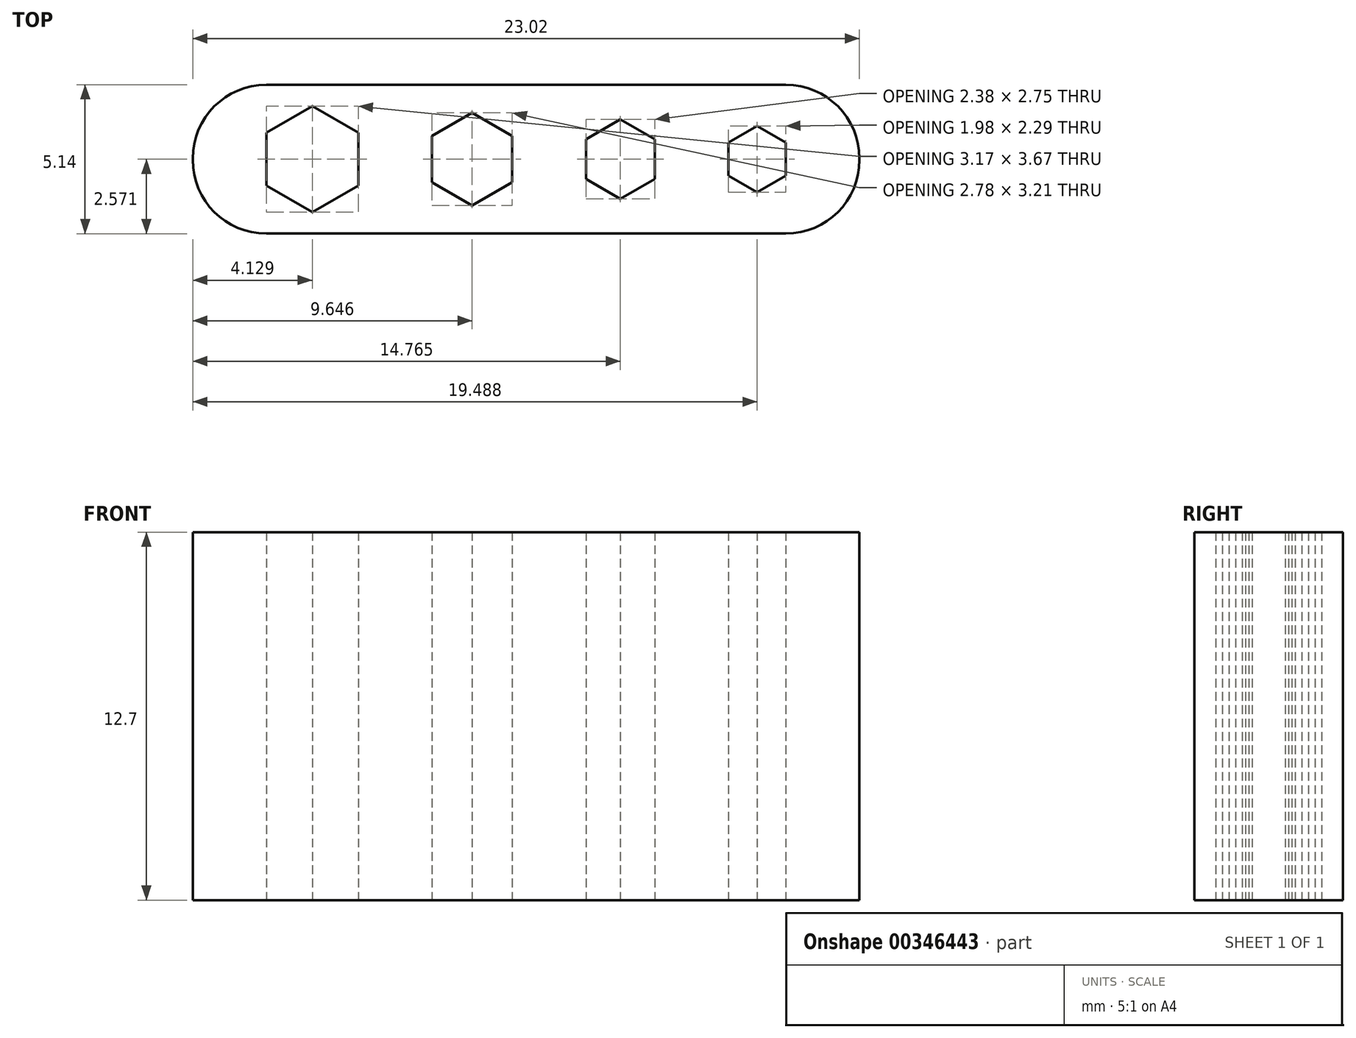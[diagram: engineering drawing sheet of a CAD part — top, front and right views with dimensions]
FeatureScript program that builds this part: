
annotation { "Feature Type Name" : "Feature", "Feature Type Description" : "" }
export const myFeature = defineFeature(function(context is Context, id is Id, definition is map)
    precondition{}
    {
        {
            var Q0;
            Q0=qCreatedBy(makeId("Top.planeOp"),FACE);
            var sketch = newSketch(context, id + "F0", { "sketchPlane" : qUnion([Q0])});
            skLineSegment(sketch, "E0.bottom", {"start": v(7.75, 15.33) * mm, "end": v(30.77, 15.33) * mm});
            skLineSegment(sketch, "E0.top", {"start": v(7.75, 10.2) * mm, "end": v(30.77, 10.2) * mm});
            skLineSegment(sketch, "E0.left", {"start": v(7.75, 15.33) * mm, "end": v(7.75, 10.2) * mm});
            skLineSegment(sketch, "E0.right", {"start": v(30.77, 15.33) * mm, "end": v(30.77, 10.2) * mm});
            skPoint(sketch, "E1.cCircle.centerSnap0", {"position": v(7.75, 12.76) * mm});
            skCircle(sketch, "E2.cCircle", {"center": v(22.52, 12.76) * mm, "radius": 1.2 * mm, "construction": true});
            skLineSegment(sketch, "E2.0", {"start": v(23.7, 13.45) * mm, "end": v(23.7, 12.07) * mm});
            skLineSegment(sketch, "E2.1", {"start": v(23.7, 12.07) * mm, "end": v(22.52, 11.39) * mm});
            skLineSegment(sketch, "E2.2", {"start": v(22.52, 11.39) * mm, "end": v(21.32, 12.07) * mm});
            skLineSegment(sketch, "E2.3", {"start": v(21.32, 12.07) * mm, "end": v(21.32, 13.45) * mm});
            skLineSegment(sketch, "E2.4", {"start": v(21.32, 13.45) * mm, "end": v(22.52, 14.14) * mm});
            skLineSegment(sketch, "E2.5", {"start": v(22.52, 14.14) * mm, "end": v(23.7, 13.45) * mm});
            skPoint(sketch, "E2.0.midPoint", {"position": v(23.7, 12.76) * mm});
            skCircle(sketch, "E3.cCircle", {"center": v(27.24, 12.76) * mm, "radius": 1 * mm, "construction": true});
            skLineSegment(sketch, "E3.0", {"start": v(28.23, 13.33) * mm, "end": v(28.23, 12.19) * mm});
            skLineSegment(sketch, "E3.1", {"start": v(28.23, 12.19) * mm, "end": v(27.24, 11.62) * mm});
            skLineSegment(sketch, "E3.2", {"start": v(27.24, 11.62) * mm, "end": v(26.25, 12.19) * mm});
            skLineSegment(sketch, "E3.3", {"start": v(26.25, 12.19) * mm, "end": v(26.25, 13.33) * mm});
            skLineSegment(sketch, "E3.4", {"start": v(26.25, 13.33) * mm, "end": v(27.24, 13.9) * mm});
            skLineSegment(sketch, "E3.5", {"start": v(27.24, 13.9) * mm, "end": v(28.23, 13.33) * mm});
            skPoint(sketch, "E3.0.midPoint", {"position": v(28.23, 12.76) * mm});
            skCircle(sketch, "E4.cCircle", {"center": v(11.88, 12.76) * mm, "radius": 1.59 * mm, "construction": true});
            skLineSegment(sketch, "E4.0", {"start": v(13.47, 13.68) * mm, "end": v(13.47, 11.84) * mm});
            skLineSegment(sketch, "E4.1", {"start": v(13.47, 11.84) * mm, "end": v(11.88, 10.93) * mm});
            skLineSegment(sketch, "E4.2", {"start": v(11.88, 10.93) * mm, "end": v(10.3, 11.84) * mm});
            skLineSegment(sketch, "E4.3", {"start": v(10.3, 11.84) * mm, "end": v(10.3, 13.68) * mm});
            skLineSegment(sketch, "E4.4", {"start": v(10.3, 13.68) * mm, "end": v(11.88, 14.6) * mm});
            skLineSegment(sketch, "E4.5", {"start": v(11.88, 14.6) * mm, "end": v(13.47, 13.68) * mm});
            skPoint(sketch, "E4.0.midPoint", {"position": v(13.47, 12.76) * mm});
            skCircle(sketch, "E5.cCircle", {"center": v(17.4, 12.76) * mm, "radius": 1.39 * mm, "construction": true});
            skLineSegment(sketch, "E5.0", {"start": v(18.78, 13.56) * mm, "end": v(18.78, 11.96) * mm});
            skLineSegment(sketch, "E5.1", {"start": v(18.78, 11.96) * mm, "end": v(17.4, 11.16) * mm});
            skLineSegment(sketch, "E5.2", {"start": v(17.4, 11.16) * mm, "end": v(16, 11.96) * mm});
            skLineSegment(sketch, "E5.3", {"start": v(16, 11.96) * mm, "end": v(16, 13.56) * mm});
            skLineSegment(sketch, "E5.4", {"start": v(16, 13.56) * mm, "end": v(17.4, 14.36) * mm});
            skLineSegment(sketch, "E5.5", {"start": v(17.4, 14.36) * mm, "end": v(18.78, 13.56) * mm});
            skPoint(sketch, "E5.0.midPoint", {"position": v(18.78, 12.76) * mm});
            skSolve(sketch);
        }
        {
            var Q0;
            Q0 = qSketchRegion(id + "F0", true);
            extrude(context, id + "F1", {"entities" : qUnion([Q0]), "depth" : 12.7 * mm});
        }
        {
            var Q0;
            Q0=makeQuery(id+"F1.opExtrude","SWEPT_EDGE",EDGE,{"disambiguationData":[OSD([sQuery(id+"F0.wireOp",EDGE,"E0.top"),sQuery(id+"F0.wireOp",EDGE,"E0.right")])]});
            var Q1;
            Q1=makeQuery(id+"F1.opExtrude","SWEPT_EDGE",EDGE,{"disambiguationData":[OSD([sQuery(id+"F0.wireOp",EDGE,"E0.top"),sQuery(id+"F0.wireOp",EDGE,"E0.left")])]});
            var Q2;
            Q2=makeQuery(id+"F1.opExtrude","SWEPT_EDGE",EDGE,{"disambiguationData":[OSD([sQuery(id+"F0.wireOp",EDGE,"E0.bottom"),sQuery(id+"F0.wireOp",EDGE,"E0.left")])]});
            var Q3;
            Q3=makeQuery(id+"F1.opExtrude","SWEPT_EDGE",EDGE,{"disambiguationData":[OSD([sQuery(id+"F0.wireOp",EDGE,"E0.bottom"),sQuery(id+"F0.wireOp",EDGE,"E0.right")])]});
            fillet(context, id + "F2", {"entities" : qUnion([Q0, Q1, Q2, Q3]), "radius" : 2.54 * mm, "tangentPropagation" : true, "allowEdgeOverflow" : false});
        }
    });
